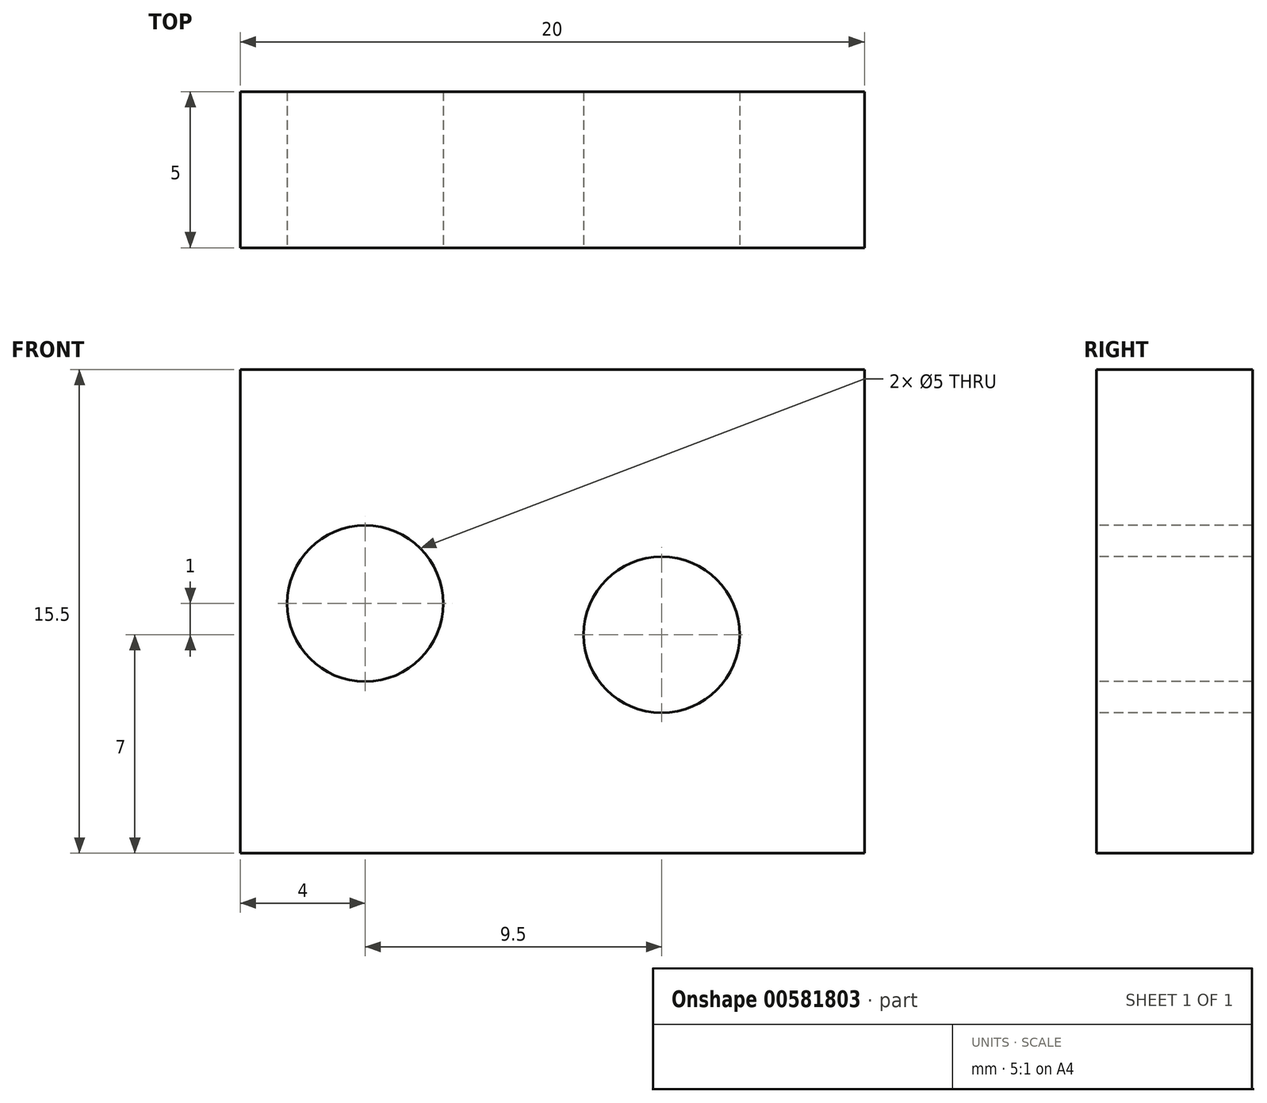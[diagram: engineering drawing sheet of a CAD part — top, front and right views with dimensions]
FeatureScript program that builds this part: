
annotation { "Feature Type Name" : "Feature", "Feature Type Description" : "" }
export const myFeature = defineFeature(function(context is Context, id is Id, definition is map)
    precondition{}
    {
        {
            var Q0;
            Q0=qCreatedBy(makeId("Front.planeOp"),FACE);
            var sketch = newSketch(context, id + "F0", { "sketchPlane" : qUnion([Q0])});
            skLineSegment(sketch, "E0.bottom", {"start": v(10, -7.75) * mm, "end": v(-10, -7.75) * mm});
            skLineSegment(sketch, "E0.top", {"start": v(10, 7.75) * mm, "end": v(-10, 7.75) * mm});
            skLineSegment(sketch, "E0.left", {"start": v(10, -7.75) * mm, "end": v(10, 7.75) * mm});
            skLineSegment(sketch, "E0.right", {"start": v(-10, -7.75) * mm, "end": v(-10, 7.75) * mm});
            skPoint(sketch, "E0.middle", {"position": v(0, 0) * mm});
            skSolve(sketch);
        }
        {
            var Q0;
            Q0=makeQuery(id+"F0.imprint","IMPRINT",FACE,{"disambiguationData":[TD([[makeQuery(id+"F0.imprint","IMPRINT",EDGE,{"derivedFrom":sQuery(id+"F0.wireOp",EDGE,"E0.bottom")}),-1.0]])]});
            extrude(context, id + "F1", {"entities" : qUnion([Q0]), "depth" : 5 * mm, "offsetDistance" : 25 * mm});
        }
        {
            var Q0;
            Q0=makeQuery(id+"F1.opExtrude","CAP_FACE",FACE,{"disambiguationData":[OSD([sQuery(id+"F0.wireOp",EDGE,"E0.bottom"),sQuery(id+"F0.wireOp",EDGE,"E0.top"),sQuery(id+"F0.wireOp",EDGE,"E0.left"),sQuery(id+"F0.wireOp",EDGE,"E0.right")])],"isStart":false});
            var sketch = newSketch(context, id + "F2", { "sketchPlane" : qUnion([Q0])});
            skCircle(sketch, "E1", {"center": v(-6, 0.25) * mm, "radius": 2.5 * mm});
            skCircle(sketch, "E2", {"center": v(3.5, -0.75) * mm, "radius": 2.5 * mm});
            skSolve(sketch);
        }
        {
            var Q0;
            Q0=makeQuery(id+"F2.imprint","IMPRINT",FACE,{"disambiguationData":[TD([[makeQuery(id+"F2.imprint","IMPRINT",EDGE,{"derivedFrom":sQuery(id+"F2.wireOp",EDGE,"E1")}),1.0]])]});
            extrude(context, id + "F3", {"entities" : qUnion([Q0]), "operationType" : NewBodyOperationType.REMOVE, "oppositeDirection" : true, "depth" : 25 * mm, "offsetDistance" : 25 * mm});
        }
        {
            var Q0;
            Q0=makeQuery(id+"F2.imprint","IMPRINT",FACE,{"disambiguationData":[TD([[makeQuery(id+"F2.imprint","IMPRINT",EDGE,{"derivedFrom":sQuery(id+"F2.wireOp",EDGE,"E2")}),1.0]])]});
            extrude(context, id + "F4", {"entities" : qUnion([Q0]), "operationType" : NewBodyOperationType.REMOVE, "oppositeDirection" : true, "depth" : 25 * mm, "offsetDistance" : 25 * mm});
        }
    });
